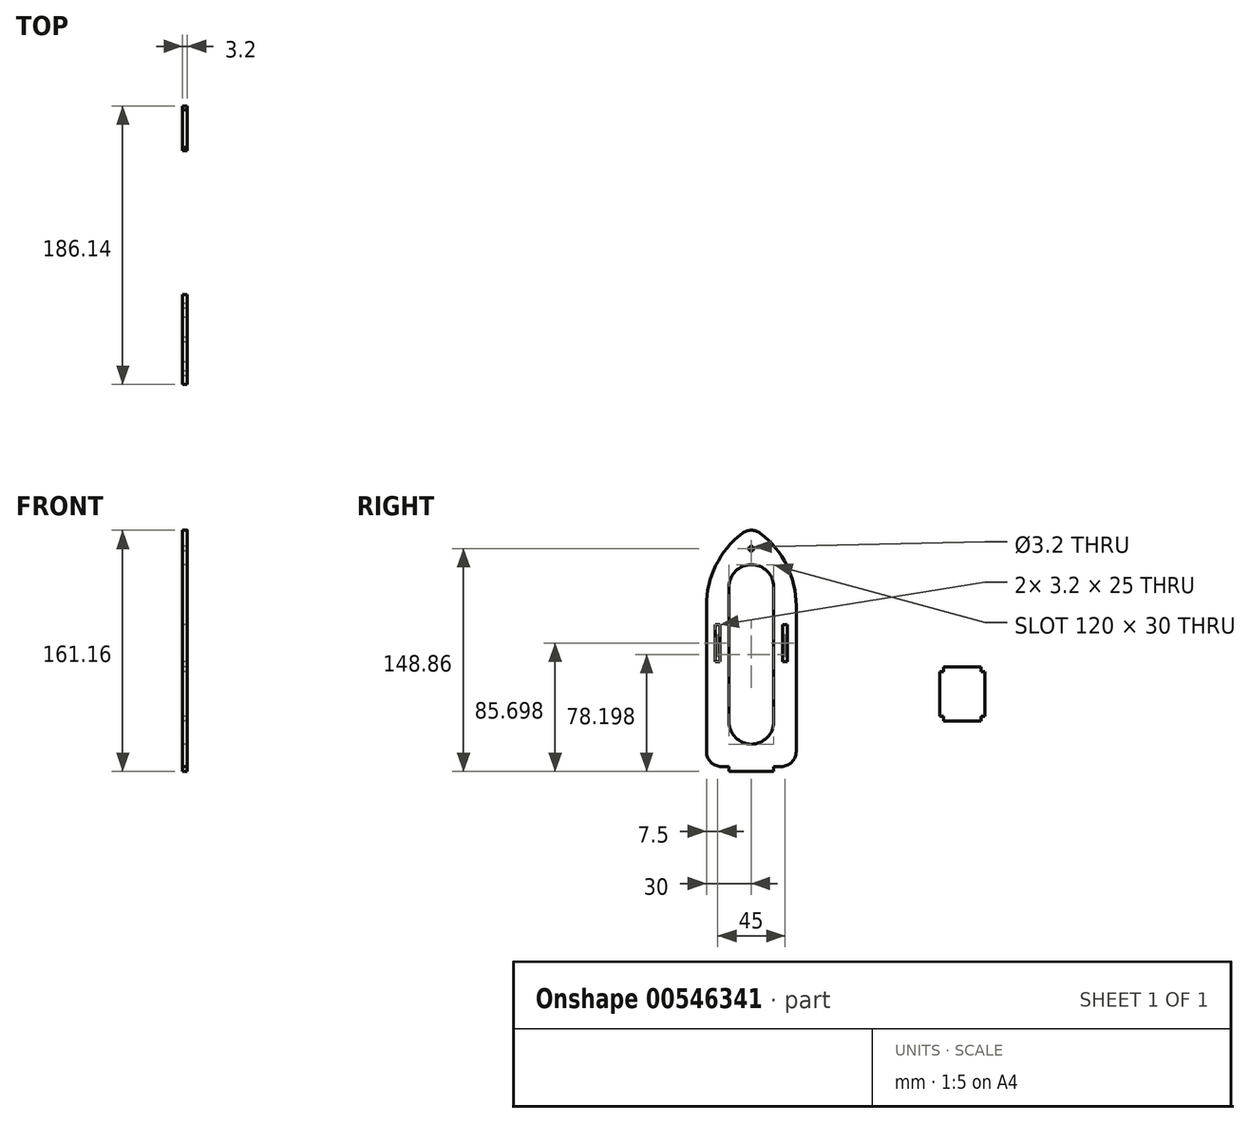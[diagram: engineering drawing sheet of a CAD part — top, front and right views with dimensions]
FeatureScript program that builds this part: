
annotation { "Feature Type Name" : "Feature", "Feature Type Description" : "" }
export const myFeature = defineFeature(function(context is Context, id is Id, definition is map)
    precondition{}
    {
        {
            var Q0;
            Q0=qCreatedBy(makeId("Right.planeOp"),FACE);
            var sketch = newSketch(context, id + "F0", { "sketchPlane" : qUnion([Q0])});
            skLineSegment(sketch, "E0.bottom", {"start": v(-20.9, 116.5) * mm, "end": v(-20.9, 116.5) * mm});
            skLineSegment(sketch, "E0.top", {"start": v(-50.9, -33.5) * mm, "end": v(-35.9, -33.5) * mm});
            skLineSegment(sketch, "E0.left", {"start": v(-50.9, 73.97) * mm, "end": v(-50.9, -33.5) * mm});
            skLineSegment(sketch, "E0.right", {"start": v(9.1, 73.97) * mm, "end": v(9.1, -33.5) * mm});
            skLineSegment(sketch, "E1.bottom", {"start": v(-20.9, 101.5) * mm, "end": v(-20.9, 101.5) * mm});
            skLineSegment(sketch, "E1.top", {"start": v(-20.9, -18.5) * mm, "end": v(-20.9, -18.5) * mm});
            skLineSegment(sketch, "E1.left", {"start": v(-35.9, 86.5) * mm, "end": v(-35.9, -3.5) * mm});
            skLineSegment(sketch, "E1.right", {"start": v(-5.9, 86.5) * mm, "end": v(-5.9, -3.5) * mm});
            skPoint(sketch, "E2.visualSharp", {"position": v(-50.9, 116.5) * mm});
            skPoint(sketch, "E3.visualSharp", {"position": v(9.1, 116.5) * mm});
            skPoint(sketch, "E4.visualSharp", {"position": v(-50.9, -33.5) * mm});
            skLineSegment(sketch, "E4.filletArc", {"start": v(-50.9, -33.5) * mm, "end": v(-50.9, -33.5) * mm});
            skPoint(sketch, "E5.visualSharp", {"position": v(9.1, -33.5) * mm});
            skLineSegment(sketch, "E5.filletArc", {"start": v(9.1, -33.5) * mm, "end": v(9.1, -33.5) * mm});
            skPoint(sketch, "E6.visualSharp", {"position": v(-35.9, 101.5) * mm});
            skArc(sketch, "E6.filletArc", {"start": v(-20.9, 101.5) * mm, "mid": v(-31.5, 97.1) * mm, "end": v(-35.9, 86.5) * mm});
            skPoint(sketch, "E7.visualSharp", {"position": v(-5.9, 101.5) * mm});
            skArc(sketch, "E7.filletArc", {"start": v(-5.9, 86.5) * mm, "mid": v(-10.3, 97.1) * mm, "end": v(-20.9, 101.5) * mm});
            skPoint(sketch, "E8.visualSharp", {"position": v(-5.9, -18.5) * mm});
            skArc(sketch, "E8.filletArc", {"start": v(-20.9, -18.5) * mm, "mid": v(-10.3, -14.1) * mm, "end": v(-5.9, -3.5) * mm});
            skPoint(sketch, "E9.visualSharp", {"position": v(-35.9, -18.5) * mm});
            skArc(sketch, "E9.filletArc", {"start": v(-35.9, -3.5) * mm, "mid": v(-31.5, -14.1) * mm, "end": v(-20.9, -18.5) * mm});
            skArc(sketch, "E10", {"start": v(9.1, 73.97) * mm, "mid": v(2.8, 100.98) * mm, "end": v(-14.82, 122.4) * mm});
            skArc(sketch, "E11", {"start": v(-26.98, 122.4) * mm, "mid": v(-44.6, 100.98) * mm, "end": v(-50.9, 73.97) * mm});
            skPoint(sketch, "E12.visualSharp", {"position": v(-20.9, 126.5) * mm});
            skArc(sketch, "E12.filletArc", {"start": v(-14.82, 122.4) * mm, "mid": v(-20.9, 124.46) * mm, "end": v(-26.98, 122.4) * mm});
            skCircle(sketch, "E13", {"center": v(-20.9, 112.16) * mm, "radius": 1.6 * mm});
            skLineSegment(sketch, "E14", {"start": v(-35.9, -33.5) * mm, "end": v(-35.9, -36.7) * mm});
            skLineSegment(sketch, "E15", {"start": v(-35.9, -36.7) * mm, "end": v(-5.9, -36.7) * mm});
            skLineSegment(sketch, "E16", {"start": v(-5.9, -36.7) * mm, "end": v(-5.9, -33.5) * mm});
            skLineSegment(sketch, "E17.trimOffspring", {"start": v(-5.9, -33.5) * mm, "end": v(9.1, -33.5) * mm});
            skLineSegment(sketch, "E18.bottom", {"start": v(0, 61.5) * mm, "end": v(3.2, 61.5) * mm});
            skLineSegment(sketch, "E18.top", {"start": v(0, 36.5) * mm, "end": v(3.2, 36.5) * mm});
            skLineSegment(sketch, "E18.left", {"start": v(0, 61.5) * mm, "end": v(0, 36.5) * mm});
            skLineSegment(sketch, "E18.right", {"start": v(3.2, 61.5) * mm, "end": v(3.2, 36.5) * mm});
            skLineSegment(sketch, "E19.bottom", {"start": v(-45, 61.5) * mm, "end": v(-41.8, 61.5) * mm});
            skLineSegment(sketch, "E19.top", {"start": v(-45, 36.5) * mm, "end": v(-41.8, 36.5) * mm});
            skLineSegment(sketch, "E19.left", {"start": v(-45, 61.5) * mm, "end": v(-45, 36.5) * mm});
            skLineSegment(sketch, "E19.right", {"start": v(-41.8, 61.5) * mm, "end": v(-41.8, 36.5) * mm});
            skLineSegment(sketch, "E20.bottom", {"start": v(105.24, 30) * mm, "end": v(107.74, 30) * mm});
            skLineSegment(sketch, "E20.top", {"start": v(105.24, 0) * mm, "end": v(107.74, 0) * mm});
            skLineSegment(sketch, "E20.left", {"start": v(105.24, 30) * mm, "end": v(105.24, 0) * mm});
            skLineSegment(sketch, "E20.right", {"start": v(135.24, 30) * mm, "end": v(135.24, 0) * mm});
            skLineSegment(sketch, "E21", {"start": v(107.74, 30) * mm, "end": v(107.74, 33.2) * mm});
            skLineSegment(sketch, "E22", {"start": v(107.74, 33.2) * mm, "end": v(132.74, 33.2) * mm});
            skLineSegment(sketch, "E23", {"start": v(132.74, 33.2) * mm, "end": v(132.74, 30) * mm});
            skLineSegment(sketch, "E24", {"start": v(132.74, 0) * mm, "end": v(132.74, -3.2) * mm});
            skLineSegment(sketch, "E25", {"start": v(132.74, -3.2) * mm, "end": v(107.74, -3.2) * mm});
            skLineSegment(sketch, "E26", {"start": v(107.74, -3.2) * mm, "end": v(107.74, 0) * mm});
            skLineSegment(sketch, "E27.trimOffspring", {"start": v(132.74, 30) * mm, "end": v(135.24, 30) * mm});
            skLineSegment(sketch, "E28.trimOffspring", {"start": v(132.74, 0) * mm, "end": v(135.24, 0) * mm});
            skSolve(sketch);
        }
        {
            var Q0;
            Q0 = qSketchRegion(id + "F0", true);
            extrude(context, id + "F1", {"entities" : qUnion([Q0]), "depth" : 3.2 * mm, "offsetDistance" : 25 * mm});
        }
        {
            var Q0;
            Q0=makeQuery(id+"F1.opExtrude","SWEPT_EDGE",EDGE,{"disambiguationData":[OSD([sQuery(id+"F0.wireOp",EDGE,"E0.top"),sQuery(id+"F0.wireOp",EDGE,"E0.left")])]});
            var Q1;
            Q1=makeQuery(id+"F1.opExtrude","SWEPT_EDGE",EDGE,{"disambiguationData":[OSD([sQuery(id+"F0.wireOp",EDGE,"E0.right"),sQuery(id+"F0.wireOp",EDGE,"E17.trimOffspring")])]});
            fillet(context, id + "F2", {"entities" : qUnion([Q0, Q1]), "radius" : 10 * mm, "tangentPropagation" : true, "allowEdgeOverflow" : false});
        }
    });
